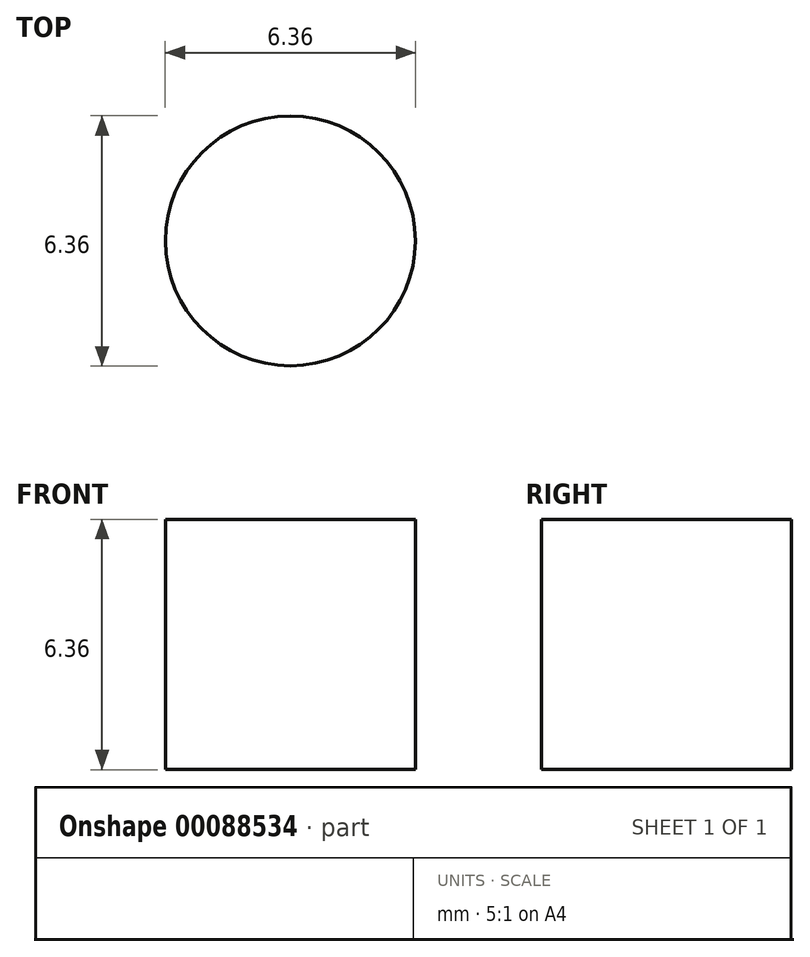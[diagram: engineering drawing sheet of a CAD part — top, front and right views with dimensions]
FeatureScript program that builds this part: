
annotation { "Feature Type Name" : "Feature", "Feature Type Description" : "" }
export const myFeature = defineFeature(function(context is Context, id is Id, definition is map)
    precondition{}
    {
        {
            var Q0;
            Q0=qCreatedBy(makeId("Top.planeOp"),FACE);
            var sketch = newSketch(context, id + "F0", { "sketchPlane" : qUnion([Q0])});
            skCircle(sketch, "E0", {"center": v(0, 0) * mm, "radius": 3.17 * mm});
            skSolve(sketch);
        }
        {
            var Q0;
            Q0 = qSketchRegion(id + "F0", true);
            extrude(context, id + "F1", {"entities" : qUnion([Q0]), "endBound" : BoundingType.SYMMETRIC, "depth" : 6.35 * mm});
        }
    });
